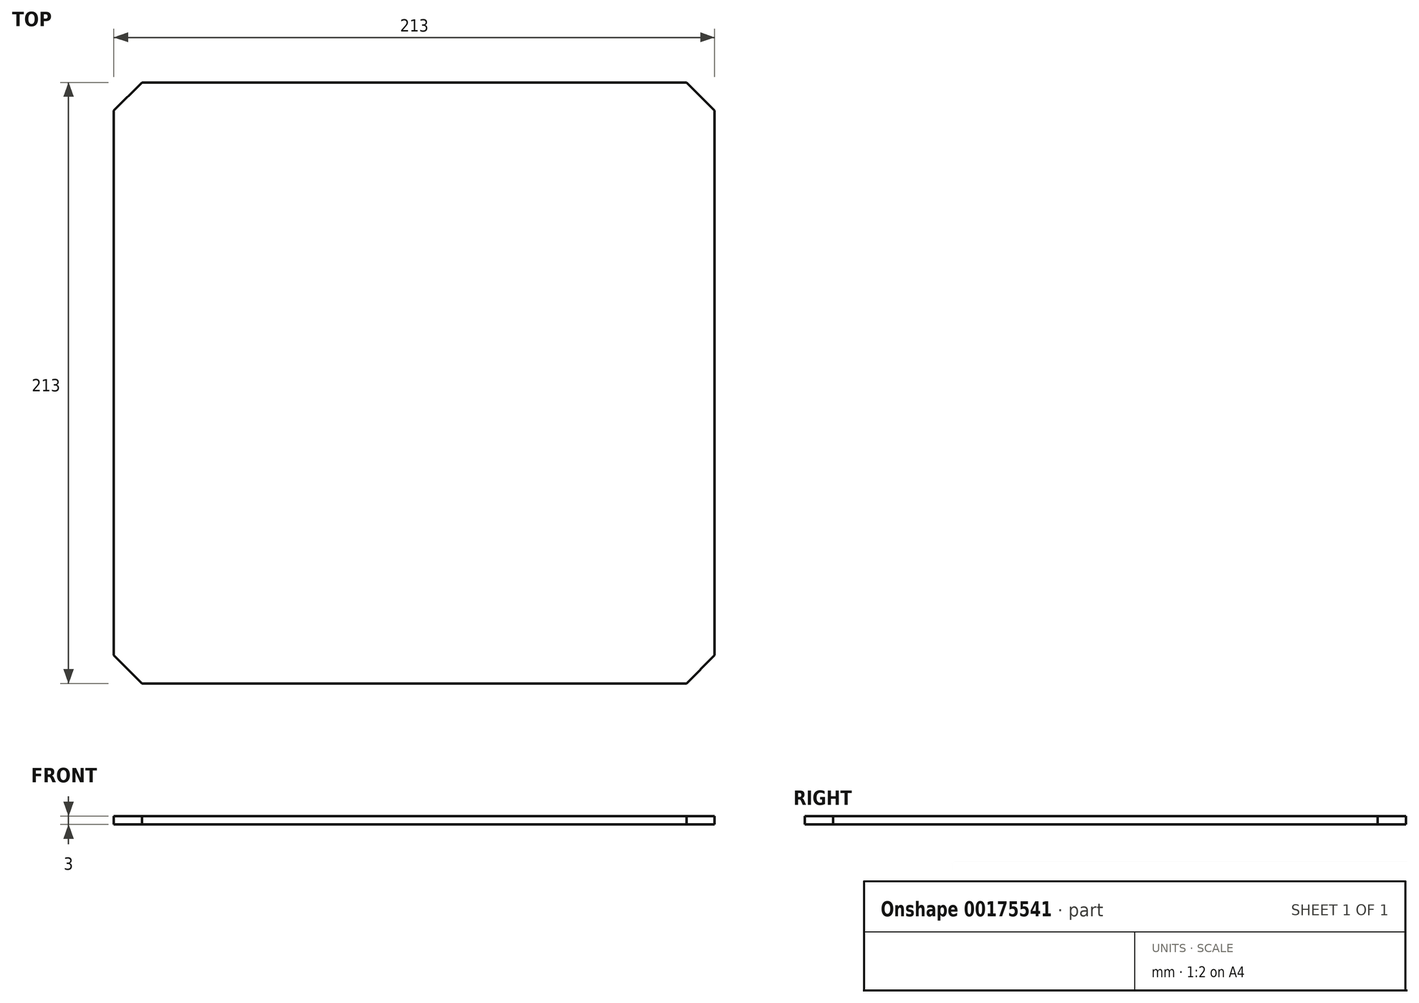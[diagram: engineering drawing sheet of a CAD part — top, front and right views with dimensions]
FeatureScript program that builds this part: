
annotation { "Feature Type Name" : "Feature", "Feature Type Description" : "" }
export const myFeature = defineFeature(function(context is Context, id is Id, definition is map)
    precondition{}
    {
        {
            var Q0;
            Q0=qCreatedBy(makeId("Top.planeOp"),FACE);
            var sketch = newSketch(context, id + "F0", { "sketchPlane" : qUnion([Q0])});
            skLineSegment(sketch, "E0", {"start": v(0, 0) * mm, "end": v(0, 147.7) * mm, "construction": true});
            skLineSegment(sketch, "E1", {"start": v(0, 0) * mm, "end": v(-171.19, 0) * mm, "construction": true});
            skLineSegment(sketch, "E2", {"start": v(-106.5, 0) * mm, "end": v(-106.5, 96.5) * mm});
            skLineSegment(sketch, "E3", {"start": v(-106.5, 96.5) * mm, "end": v(-96.5, 106.5) * mm});
            skLineSegment(sketch, "E4", {"start": v(-96.5, 106.5) * mm, "end": v(0, 106.5) * mm});
            skLineSegment(sketch, "E5.MirrorCS", {"start": v(106.5, 96.5) * mm, "end": v(96.5, 106.5) * mm});
            skLineSegment(sketch, "E6.MirrorCS", {"start": v(106.5, 0) * mm, "end": v(106.5, 96.5) * mm});
            skLineSegment(sketch, "E7.MirrorCS", {"start": v(96.5, 106.5) * mm, "end": v(0, 106.5) * mm});
            skLineSegment(sketch, "E8.MirrorCS", {"start": v(106.5, -96.5) * mm, "end": v(96.5, -106.5) * mm});
            skLineSegment(sketch, "E9.MirrorCS", {"start": v(-106.5, -96.5) * mm, "end": v(-96.5, -106.5) * mm});
            skLineSegment(sketch, "E10.MirrorCS", {"start": v(-106.5, 0) * mm, "end": v(-106.5, -96.5) * mm});
            skLineSegment(sketch, "E11.MirrorCS", {"start": v(106.5, 0) * mm, "end": v(106.5, -96.5) * mm});
            skLineSegment(sketch, "E12.MirrorCS", {"start": v(-96.5, -106.5) * mm, "end": v(0, -106.5) * mm});
            skLineSegment(sketch, "E13.MirrorCS", {"start": v(96.5, -106.5) * mm, "end": v(0, -106.5) * mm});
            skSolve(sketch);
        }
        {
            var Q0;
            Q0=makeQuery(id+"F0.imprint","IMPRINT",FACE,{"disambiguationData":[TD([[makeQuery(id+"F0.imprint","IMPRINT",EDGE,{"derivedFrom":sQuery(id+"F0.wireOp",EDGE,"E2")}),-1.0]])]});
            extrude(context, id + "F1", {"entities" : qUnion([Q0]), "depth" : 3 * mm});
        }
    });
